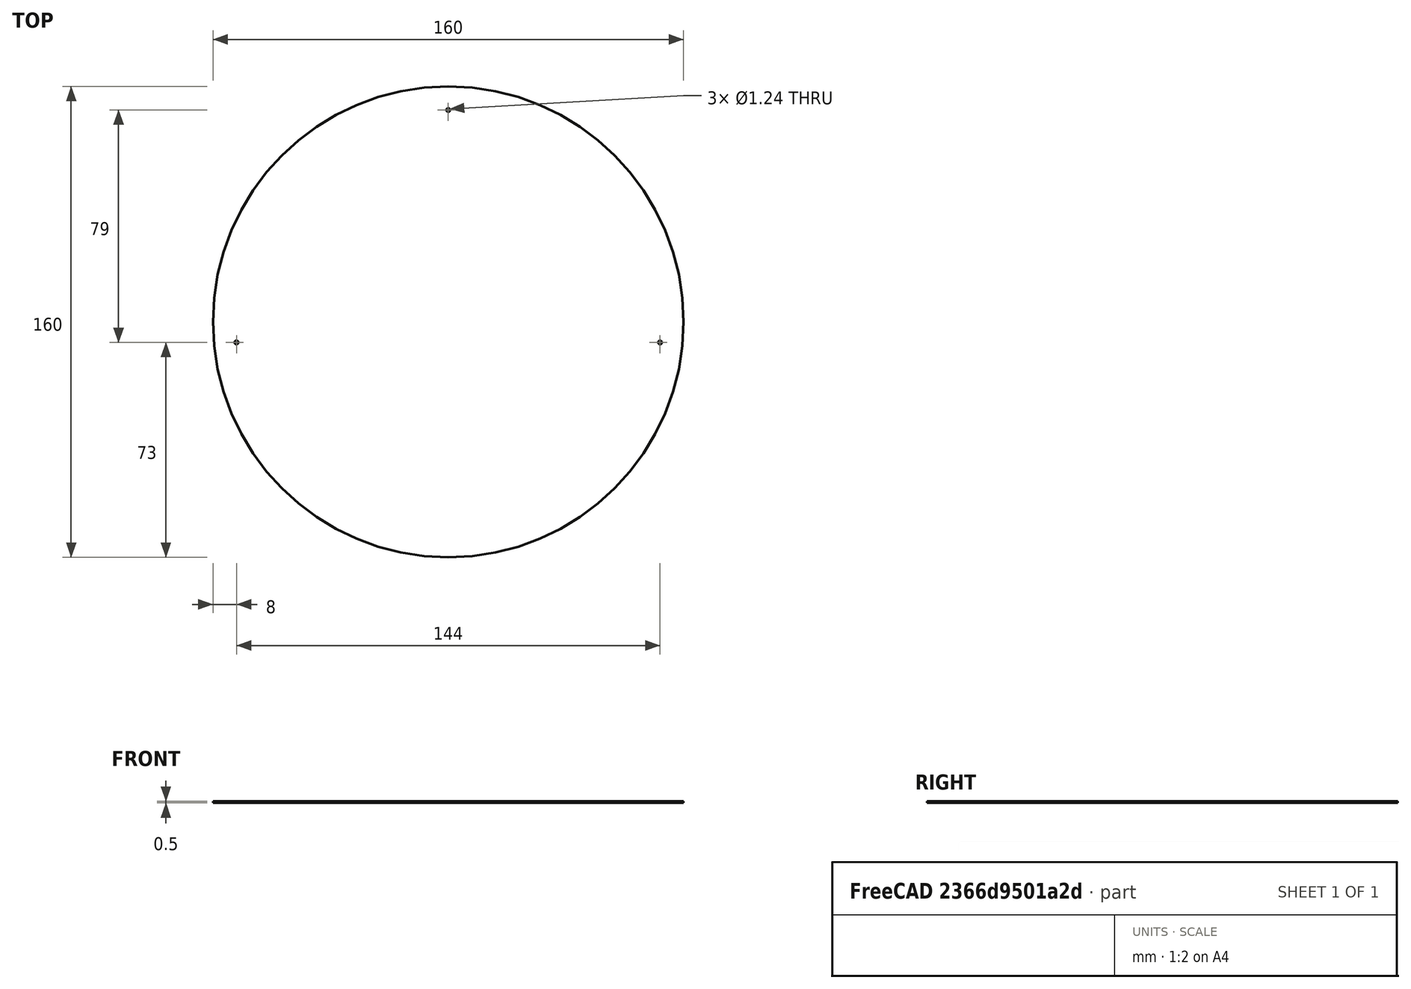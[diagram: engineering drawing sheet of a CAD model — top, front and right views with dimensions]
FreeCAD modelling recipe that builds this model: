
FCSTD DOCUMENT  (FreeCAD 0.16R6706 (Git))
Label: superficie
License: All rights reserved
LicenseURL: http://en.wikipedia.org/wiki/All_rights_reserved
objects: Part::Cylinder×4, Part::Cut×3
note: 7 computed .brp shape members not serialized (recipe doc carries the construction recipe); baked Part::Feature solids carry a one-line shape summary decoded from their .brp

FEATURE [Part::Cylinder] Cylinder  label="Cilindro"
  Angle = 360
  Height = 0.5
  Radius = 80
FEATURE [Part::Cylinder] Cylinder001  label="Cilindro001"
  Angle = 360
  Height = 0.5
  Placement = pos=(72,-7,0) rot=(0,0,-1;0.034907rad)
  Radius = 0.62
FEATURE [Part::Cylinder] Cylinder002  label="Cilindro002"
  Angle = 360
  Height = 0.5
  Placement = pos=(-72,-7,0) rot=(0,0,1;0rad)
  Radius = 0.62
FEATURE [Part::Cylinder] Cylinder003  label="Cilindro003"
  Angle = 360
  Height = 0.5
  Placement = pos=(0,72,0) rot=(0,0,1;0rad)
  Radius = 0.62
FEATURE [Part::Cut] Cut
  Base = -> Cylinder
  Tool = -> Cylinder001
FEATURE [Part::Cut] Cut001
  Base = -> Cut
  Tool = -> Cylinder002
FEATURE [Part::Cut] Cut002
  Base = -> Cut001
  Placement = pos=(0,0,-1) rot=(0,0,1;0rad)
  Tool = -> Cylinder003
